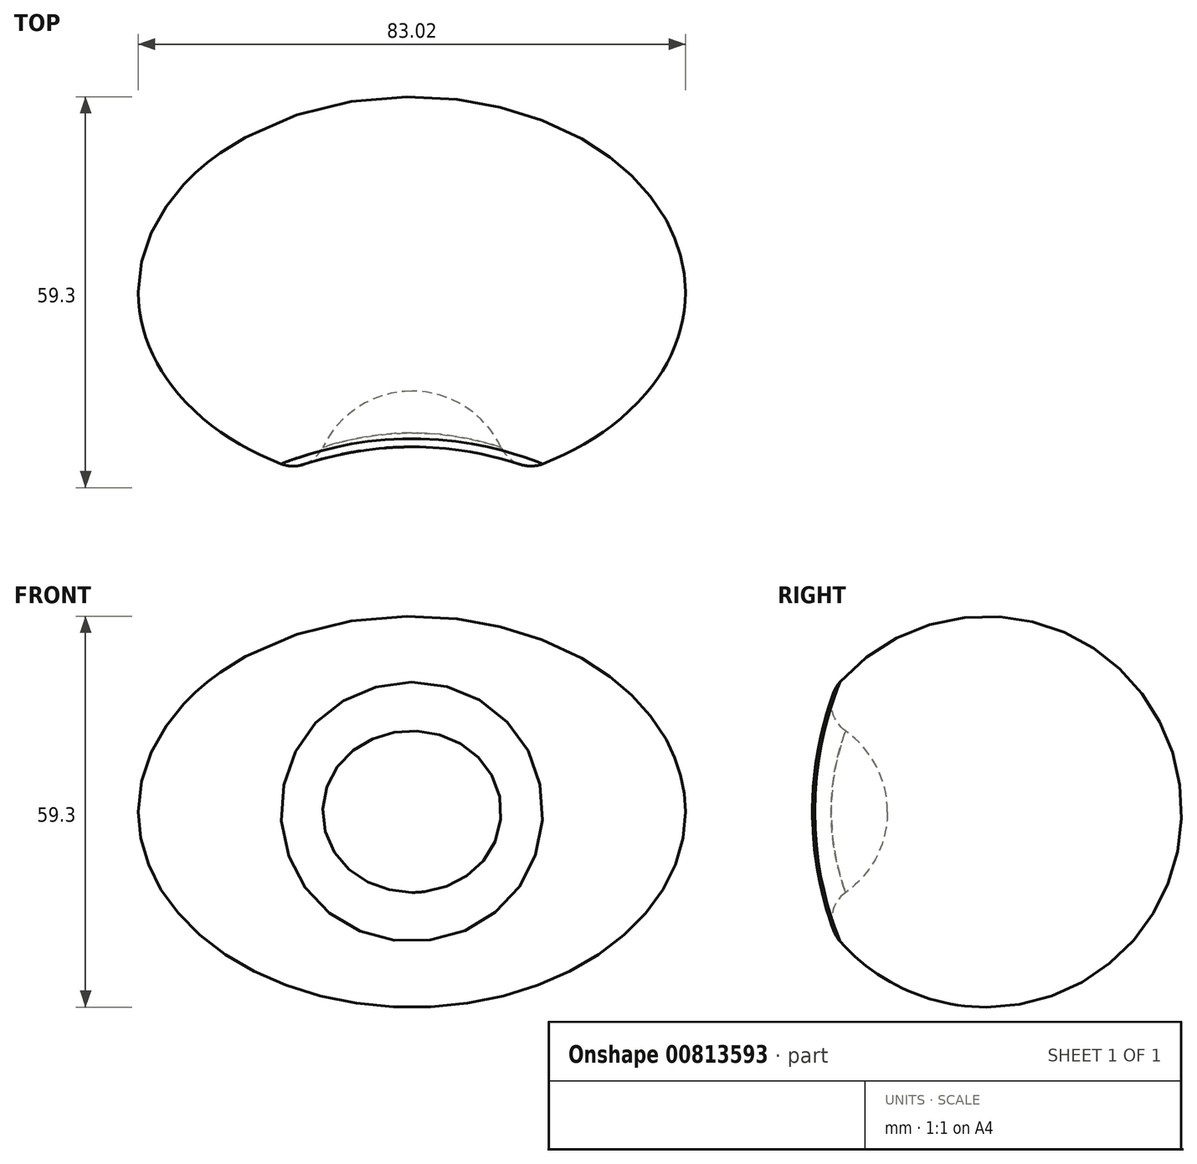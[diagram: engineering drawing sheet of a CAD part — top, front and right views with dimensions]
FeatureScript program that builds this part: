
annotation { "Feature Type Name" : "Feature", "Feature Type Description" : "" }
export const myFeature = defineFeature(function(context is Context, id is Id, definition is map)
    precondition{}
    {
        {
            var Q0;
            Q0=qCreatedBy(makeId("Front.planeOp"),FACE);
            var sketch = newSketch(context, id + "F0", { "sketchPlane" : qUnion([Q0])});
            skEllipse(sketch, "E0", {"center": v(0, 0) * mm, "majorRadius": 41.51 * mm, "minorRadius": 29.65 * mm, "majorAxis": v(1, 0)});
            skLineSegment(sketch, "E1", {"start": v(-53.3, 0) * mm, "end": v(69.44, 0) * mm});
            skSolve(sketch);
        }
        {
            var Q0;
            {var subQ0=sQuery(id+"F0.wireOp",EDGE,"E1");var subQ1=sQuery(id+"F0.wireOp",EDGE,"E0");var subQ2=makeQuery(id+"F0.imprint","INTERSECT",VERTEX,{"disambiguationData":[OD(0.0)],"derivedFrom":[subQ1,subQ0]});Q0=makeQuery(id+"F0.imprint","IMPRINT",FACE,{"disambiguationData":[TD([[makeQuery(id+"F0.imprint","IMPRINT",EDGE,{"disambiguationData":[TD([[subQ2,1.0]])],"derivedFrom":subQ1}),1.0]])]});}
            var Q1;
            Q1=sQuery(id+"F0.wireOp",EDGE,"E1");
            revolve(context, id + "F1", {"surfaceOperationType" : NewSurfaceOperationType.NEW, "entities" : qUnion([Q0]), "axis" : qUnion([Q1]), "revolveType" : RevolveType.FULL});
        }
        {
            var Q0;
            Q0=qCreatedBy(makeId("Front.planeOp"),FACE);
            cPlane(context, id + "F2", {"entities" : qUnion([Q0]), "cplaneType" : CPlaneType.OFFSET, "offset" : 15 * mm, "width" : 150 * mm, "height" : 150 * mm});
        }
        {
            var Q0;
            Q0=qCreatedBy(id+"F2.planeOp",FACE);
            var sketch = newSketch(context, id + "F3", { "sketchPlane" : qUnion([Q0])});
            skCircle(sketch, "E2", {"center": v(0, 0) * mm, "radius": 15 * mm});
            skSolve(sketch);
        }
        {
            var Q0;
            Q0 = qSketchRegion(id + "F3", true);
            extrude(context, id + "F4", {"entities" : qUnion([Q0]), "operationType" : NewBodyOperationType.REMOVE, "depth" : 25 * mm, "offsetDistance" : 25 * mm});
        }
        {
            var Q0;
            Q0=makeQuery(id+"F4.boolean.opBoolean","COPY",EDGE,{"derivedFrom":makeQuery(id+"F4.opExtrude","CAP_EDGE",EDGE,{"disambiguationData":[OSD([sQuery(id+"F3.wireOp",EDGE,"E2")])],"isStart":true})});
            fillet(context, id + "F5", {"entities" : qUnion([Q0]), "radius" : 15 * mm, "tangentPropagation" : true, "allowEdgeOverflow" : false});
        }
        {
            var Q0;
            Q0=makeQuery(id+"F5.opFillet","BLEND_FACE",FACE,{"disambiguationData":[OSD([sQuery(id+"F3.wireOp",EDGE,"E2")])]});
            fillet(context, id + "F6", {"entities" : qUnion([Q0]), "radius" : 5 * mm, "tangentPropagation" : true, "allowEdgeOverflow" : false});
        }
    });
